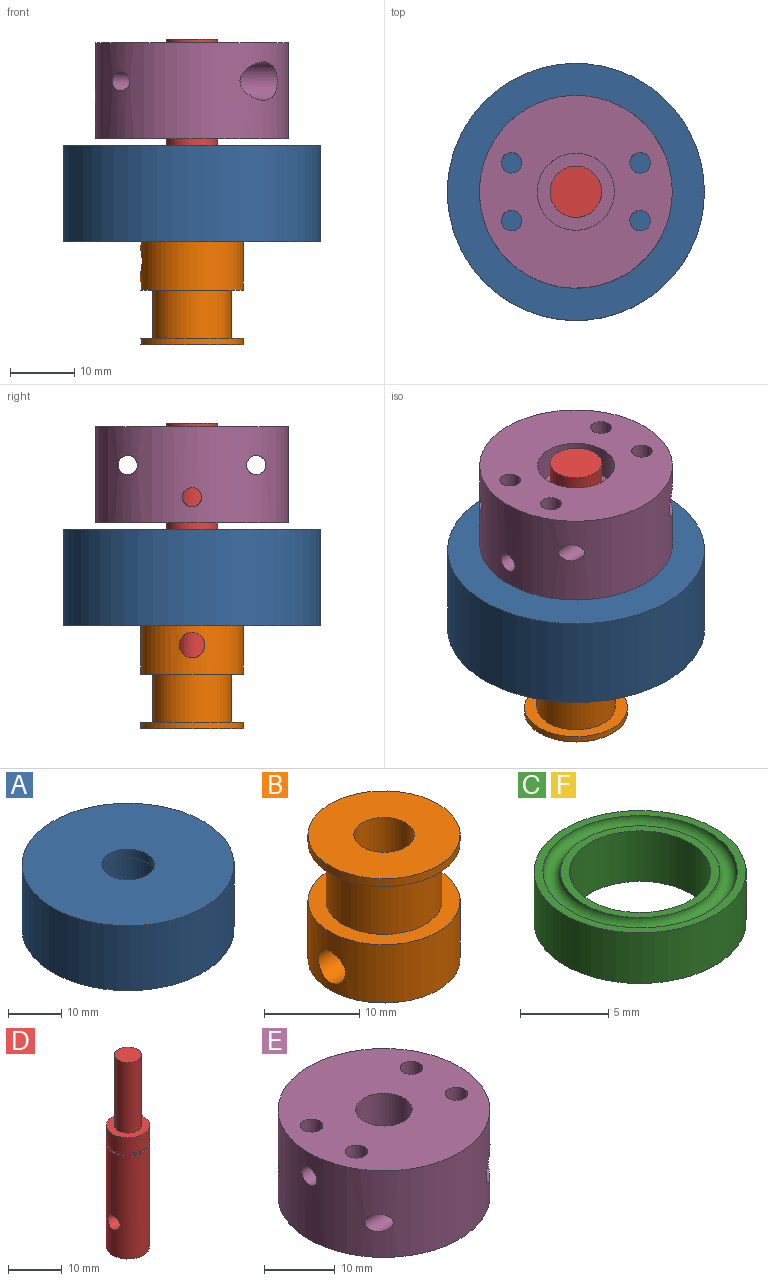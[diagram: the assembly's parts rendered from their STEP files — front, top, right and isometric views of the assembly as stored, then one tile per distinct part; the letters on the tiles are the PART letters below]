
ASSEMBLY  parts=6 mates=10
PART A: 12 faces, bbox 40x40x15 mm
  f0: cylinder r=6mm len=12mm, axis (0,0,1), area 339.3mm2, adj f6,f10
  f1: cylinder r=6mm len=12mm, axis (0,0,1), area 37.7mm2, adj f8,f9
  f2: plane 40x40mm, normal (0,0,-1), area 942.5mm2, adj f4,f7
  f3: plane 40x40mm, normal (0,0,1), area 1178.1mm2, adj f4,f5
  f4: cylinder r=20mm len=40mm, axis (0,0,1), area 1885mm2, adj f2,f3
  f5: cylinder r=5mm len=10mm, axis (0,0,1), area 62.8mm2, adj f3,f6
  f6: plane 12x12mm, normal (0,0,-1), area 34.6mm2, adj f0,f5
  f7: cylinder r=10mm len=20mm, axis (0,0,-1), area 125.7mm2, adj f2,f8
  f8: plane 20x20mm, normal (0,0,-1), area 201.1mm2, adj f1,f7
  f9: plane 12.5x12.5mm, normal (0,0,1), area 9.6mm2, adj f1,f11
  f10: plane 12.5x12.5mm, normal (0,0,-1), area 9.6mm2, adj f0,f11
  f11: cylinder r=6.25mm len=12.5mm, axis (0,0,1), area 39.3mm2, adj f9,f10
PART B: 9 faces, bbox 16x16x16 mm
  f0: cylinder r=8mm len=16mm, axis (0,0,1), area 364.3mm2, adj f1,f6,f8
  f1: plane 16x16mm, normal (0,0,-1), area 169.4mm2, adj f0,f7
  f2: plane 16x16mm, normal (0,0,1), area 169.4mm2, adj f3,f7
  f3: cylinder r=8mm len=16mm, axis (0,0,1), area 50.3mm2, adj f2,f4
  f4: plane 16x16mm, normal (0,0,-1), area 84.2mm2, adj f3,f5
  f5: cylinder r=6.1mm len=12.2mm, axis (0,0,1), area 287.5mm2, adj f4,f6
  f6: plane 16x16mm, normal (0,0,1), area 84.2mm2, adj f0,f5
  f7: cylinder r=3.17mm len=16mm, axis (0,0,-1), area 305.9mm2, adj f1,f2,f8
  f8: cylinder r=2mm len=5.53mm, axis (1,0,0), area 63.4mm2, adj f0,f7
PART C: 8 faces, bbox 12x12x4.2 mm
  f0: cylinder r=4mm len=8mm, axis (0,0,1), area 88mm2, adj f1,f7
  f1: plane 9x9mm, normal (0,0,1), area 13.4mm2, adj f0,f2
  f2: torus R=5mm, axis (0,0,1), area 49.3mm2, adj f1,f3
  f3: plane 12x12mm, normal (0,0,1), area 18.1mm2, adj f2,f4
  f4: cylinder r=6mm len=12mm, axis (0,0,1), area 131.9mm2, adj f3,f5
  f5: plane 12x12mm, normal (0,0,-1), area 18.1mm2, adj f4,f6
  f6: torus R=5mm, axis (0,0,1), area 49.3mm2, adj f5,f7
  f7: plane 9x9mm, normal (0,0,-1), area 13.4mm2, adj f0,f6
PART D: 10 faces, bbox 8x8x43.5 mm
  f0: cylinder r=4mm len=23.4mm, axis (0,0,-1), area 571.7mm2, adj f6,f8,f9
  f1: plane 8x8mm, normal (0,0,1), area 30.6mm2, adj f2,f3
  f2: cylinder r=4mm len=8mm, axis (0,0,-1), area 88mm2, adj f1,f5
  f3: cylinder r=2.5mm len=16mm, axis (0,0,-1), area 251.3mm2, adj f1,f4
  f4: plane 5x5mm, normal (0,0,1), area 19.6mm2, adj f3
  f5: plane 8x8mm, normal (0,0,-1), area 4.9mm2, adj f2,f7
  f6: plane 8x8mm, normal (0,0,1), area 4.9mm2, adj f0,f7
  f7: cylinder r=3.8mm len=7.6mm, axis (0,0,-1), area 14.3mm2, adj f5,f6
  f8: plane 8x8mm, normal (0,0,-1), area 50.3mm2, adj f0
  f9: cylinder r=1.6mm len=8mm, axis (-1,0,0), area 77.1mm2, adj f0
PART E: 17 faces, bbox 30x30x15 mm
  f0: cylinder r=1.5mm len=17.36mm, axis (-1,0,0), area 151.6mm2, adj f2,f15
  f1: cylinder r=1.5mm len=17.36mm, axis (-1,0,0), area 151.6mm2, adj f2,f13
  f2: cylinder r=15mm len=30mm, axis (0,0,1), area 1308.3mm2, adj f0,f1,f3,f4,f12,f14,f16
  f3: plane 30x30mm, normal (0,0,1), area 624.4mm2, adj f2,f7,f8,f9,f10,f11
  f4: plane 30x30mm, normal (0,0,-1), area 561.6mm2, adj f2,f5,f8,f9,f10,f11
  f5: cylinder r=6mm len=12mm, axis (0,0,1), area 188.5mm2, adj f4,f6
  f6: plane 12x12mm, normal (0,0,-1), area 62.8mm2, adj f5,f7
  f7: cylinder r=4mm len=10mm, axis (0,0,1), area 244.1mm2, adj f3,f6,f16
  f8: cylinder r=1.6mm len=15mm, axis (0,0,-1), area 150.8mm2, adj f3,f4
  f9: cylinder r=1.6mm len=15mm, axis (0,0,-1), area 150.8mm2, adj f3,f4
  f10: cylinder r=1.6mm len=15mm, axis (0,0,-1), area 150.8mm2, adj f3,f4
  f11: cylinder r=1.6mm len=15mm, axis (0,0,-1), area 150.8mm2, adj f3,f4
  f12: cylinder r=3mm len=8.27mm, axis (1,0,0), area 109.1mm2, adj f2,f13
  f13: plane 6x6mm, normal (1,0,0), area 21.2mm2, adj f1,f12
  f14: cylinder r=3mm len=8.27mm, axis (1,0,0), area 109.1mm2, adj f2,f15
  f15: plane 6x6mm, normal (1,0,0), area 21.2mm2, adj f0,f14
  f16: cylinder r=1.5mm len=11.29mm, axis (1,0,0), area 104.7mm2, adj f2,f7
PART F: same geometry as C
PLACE A t=(29.16,-17.06,-68.52)mm fixed
PLACE B rot(axis=(1,0,0),180deg) t=(29.16,-17.06,-76.52)mm
PLACE C t=(29.16,-17.06,-64.52)mm
PLACE D rot(axis=(1,0,0),180deg) t=(29.16,-17.06,-43.02)mm
PLACE E rot(axis=(1,0,0),180deg) t=(29.16,-17.06,-37.52)mm
PLACE F rot(axis=(0,0,1),90deg) t=(29.16,-17.06,-59.02)mm
MATE cylindrical B.f7 <-> D.f3  axis (0,0,1) through (29.16,-17.06,-68.52)mm
MATE planar A.f0 <-> E.f9  axis (0,0,1) through (29.16,-17.06,-53.52)mm
MATE planar B.f0 <-> A.f5  axis (0,0,1) through (29.16,-17.06,-68.52)mm
MATE cylindrical D.f0 <-> C.f0  axis (0,0,1) through (29.16,-17.06,-48.72)mm
MATE cylindrical E.f2 <-> D.f0  axis (0,0,-1) through (29.16,-17.06,-52.52)mm
MATE cylindrical C.f0 <-> A.f0  axis (0,0,1) through (29.16,-17.06,-62.77)mm
MATE cylindrical F.f0 <-> A.f5  axis (0,0,1) through (29.16,-17.06,-55.52)mm
MATE planar F.f0 <-> A.f7  axis (0,0,1) through (29.16,-17.06,-55.52)mm
MATE planar D.f0 <-> C.f0  axis (0,0,-1) through (29.16,-17.06,-64.52)mm
MATE planar C.f0 <-> A.f7  axis (0,0,-1) through (29.16,-17.06,-64.52)mm
